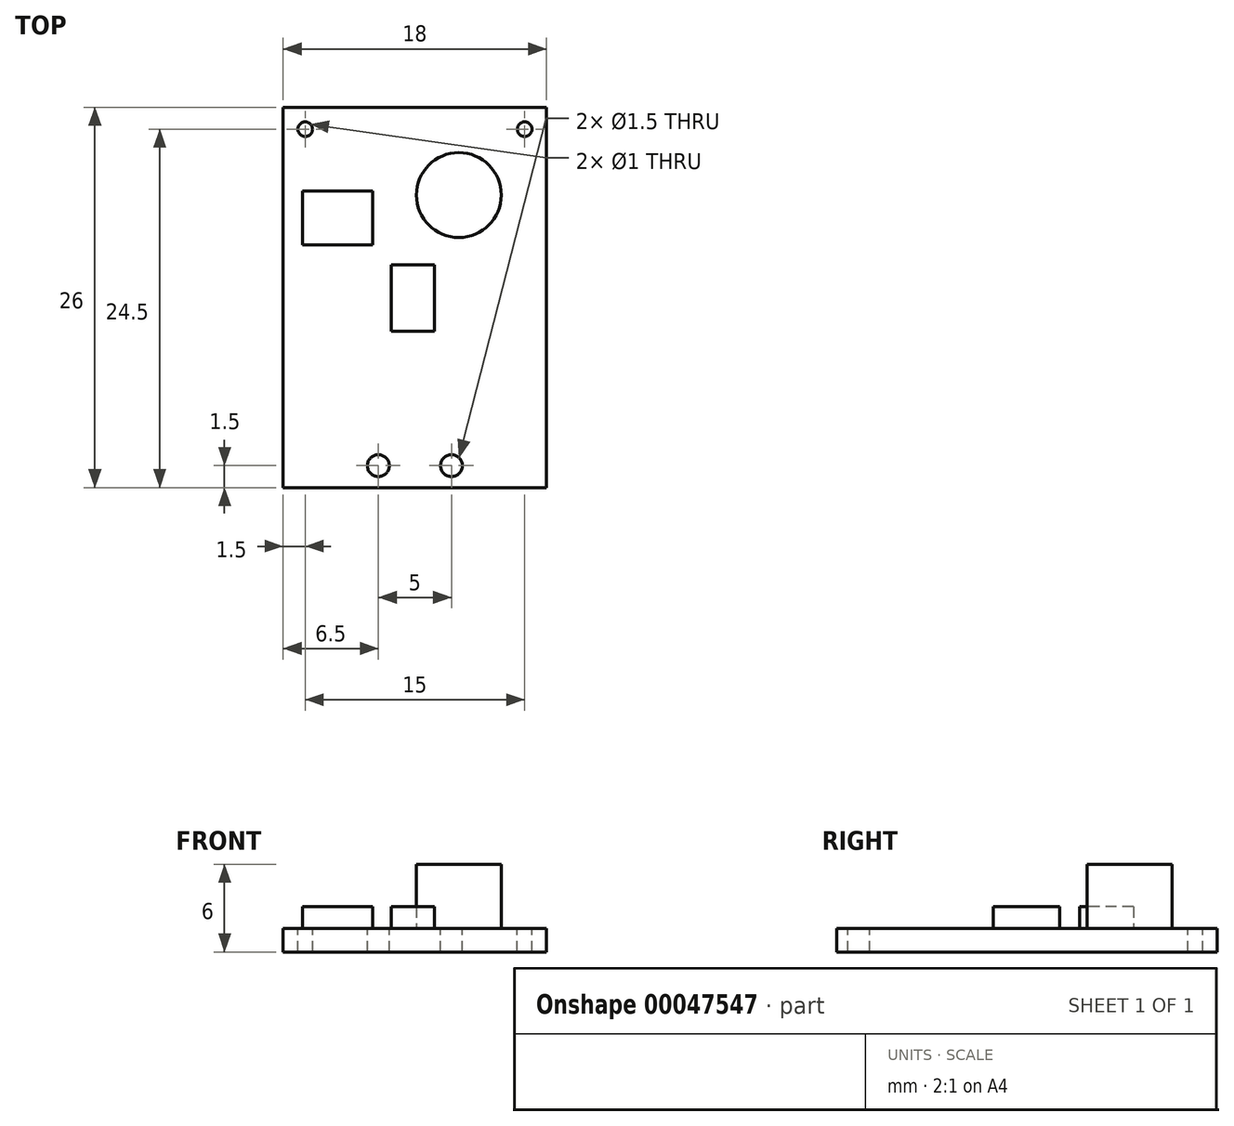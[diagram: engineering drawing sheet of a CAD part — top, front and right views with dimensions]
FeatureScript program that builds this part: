
annotation { "Feature Type Name" : "Feature", "Feature Type Description" : "" }
export const myFeature = defineFeature(function(context is Context, id is Id, definition is map)
    precondition{}
    {
        {
            var Q0;
            Q0=qCreatedBy(makeId("Top.planeOp"),FACE);
            var sketch = newSketch(context, id + "F0", { "sketchPlane" : qUnion([Q0])});
            skLineSegment(sketch, "E0.bottom", {"start": v(-9, 13) * mm, "end": v(9, 13) * mm});
            skLineSegment(sketch, "E0.top", {"start": v(-9, -13) * mm, "end": v(9, -13) * mm});
            skLineSegment(sketch, "E0.left", {"start": v(-9, 13) * mm, "end": v(-9, -13) * mm});
            skLineSegment(sketch, "E0.right", {"start": v(9, 13) * mm, "end": v(9, -13) * mm});
            skSolve(sketch);
        }
        {
            var Q0;
            Q0 = qSketchRegion(id + "F0", true);
            extrude(context, id + "F1", {"entities" : qUnion([Q0]), "depth" : 1.6 * mm});
        }
        {
            var Q0;
            Q0=makeQuery(id+"F1.opExtrude","CAP_FACE",FACE,{"disambiguationData":[OSD([sQuery(id+"F0.wireOp",EDGE,"E0.bottom"),sQuery(id+"F0.wireOp",EDGE,"E0.top"),sQuery(id+"F0.wireOp",EDGE,"E0.left"),sQuery(id+"F0.wireOp",EDGE,"E0.right")])],"isStart":false});
            var sketch = newSketch(context, id + "F2", { "sketchPlane" : qUnion([Q0])});
            skCircle(sketch, "E1", {"center": v(3, 7) * mm, "radius": 2.9 * mm});
            skSolve(sketch);
        }
        {
            var Q0;
            Q0 = qSketchRegion(id + "F2", true);
            extrude(context, id + "F3", {"entities" : qUnion([Q0]), "operationType" : NewBodyOperationType.ADD, "depth" : (6 - 1.6) * mm});
        }
        {
            var Q0;
            Q0=makeQuery(id+"F1.opExtrude","CAP_FACE",FACE,{"disambiguationData":[OSD([sQuery(id+"F0.wireOp",EDGE,"E0.bottom"),sQuery(id+"F0.wireOp",EDGE,"E0.top"),sQuery(id+"F0.wireOp",EDGE,"E0.left"),sQuery(id+"F0.wireOp",EDGE,"E0.right")])],"isStart":false});
            var sketch = newSketch(context, id + "F4", { "sketchPlane" : qUnion([Q0])});
            skLineSegment(sketch, "E2.bottom", {"start": v(-7.68, 7.27) * mm, "end": v(-2.89, 7.27) * mm});
            skLineSegment(sketch, "E2.top", {"start": v(-7.68, 3.6) * mm, "end": v(-2.89, 3.6) * mm});
            skLineSegment(sketch, "E2.left", {"start": v(-7.68, 7.27) * mm, "end": v(-7.68, 3.6) * mm});
            skLineSegment(sketch, "E2.right", {"start": v(-2.89, 7.27) * mm, "end": v(-2.89, 3.6) * mm});
            skLineSegment(sketch, "E3.bottom", {"start": v(-1.6, 2.24) * mm, "end": v(1.35, 2.24) * mm});
            skLineSegment(sketch, "E3.top", {"start": v(-1.6, -2.31) * mm, "end": v(1.35, -2.31) * mm});
            skLineSegment(sketch, "E3.left", {"start": v(-1.6, 2.24) * mm, "end": v(-1.6, -2.31) * mm});
            skLineSegment(sketch, "E3.right", {"start": v(1.35, 2.24) * mm, "end": v(1.35, -2.31) * mm});
            skSolve(sketch);
        }
        {
            var Q0;
            Q0=makeQuery(id+"F4.imprint","IMPRINT",FACE,{"disambiguationData":[TD([[makeQuery(id+"F4.imprint","IMPRINT",EDGE,{"derivedFrom":sQuery(id+"F4.wireOp",EDGE,"E2.bottom")}),-1.0]])]});
            var Q1;
            Q1=makeQuery(id+"F4.imprint","IMPRINT",FACE,{"disambiguationData":[TD([[makeQuery(id+"F4.imprint","IMPRINT",EDGE,{"derivedFrom":sQuery(id+"F4.wireOp",EDGE,"E3.bottom")}),-1.0]])]});
            extrude(context, id + "F5", {"entities" : qUnion([Q0, Q1]), "operationType" : NewBodyOperationType.ADD, "depth" : 1.5 * mm});
        }
        {
            var Q0;
            Q0=makeQuery(id+"F1.opExtrude","CAP_FACE",FACE,{"disambiguationData":[OSD([sQuery(id+"F0.wireOp",EDGE,"E0.bottom"),sQuery(id+"F0.wireOp",EDGE,"E0.top"),sQuery(id+"F0.wireOp",EDGE,"E0.left"),sQuery(id+"F0.wireOp",EDGE,"E0.right")])],"isStart":false});
            var sketch = newSketch(context, id + "F6", { "sketchPlane" : qUnion([Q0])});
            skCircle(sketch, "E4", {"center": v(-2.5, -11.5) * mm, "radius": 0.75 * mm});
            skCircle(sketch, "E5", {"center": v(2.5, -11.5) * mm, "radius": 0.75 * mm});
            skCircle(sketch, "E6", {"center": v(7.5, 11.5) * mm, "radius": 0.5 * mm});
            skCircle(sketch, "E7", {"center": v(-7.5, 11.5) * mm, "radius": 0.5 * mm});
            skSolve(sketch);
        }
        {
            var Q0;
            Q0 = qSketchRegion(id + "F6", true);
            extrude(context, id + "F7", {"entities" : qUnion([Q0]), "operationType" : NewBodyOperationType.REMOVE, "oppositeDirection" : true, "depth" : 25 * mm});
        }
    });
